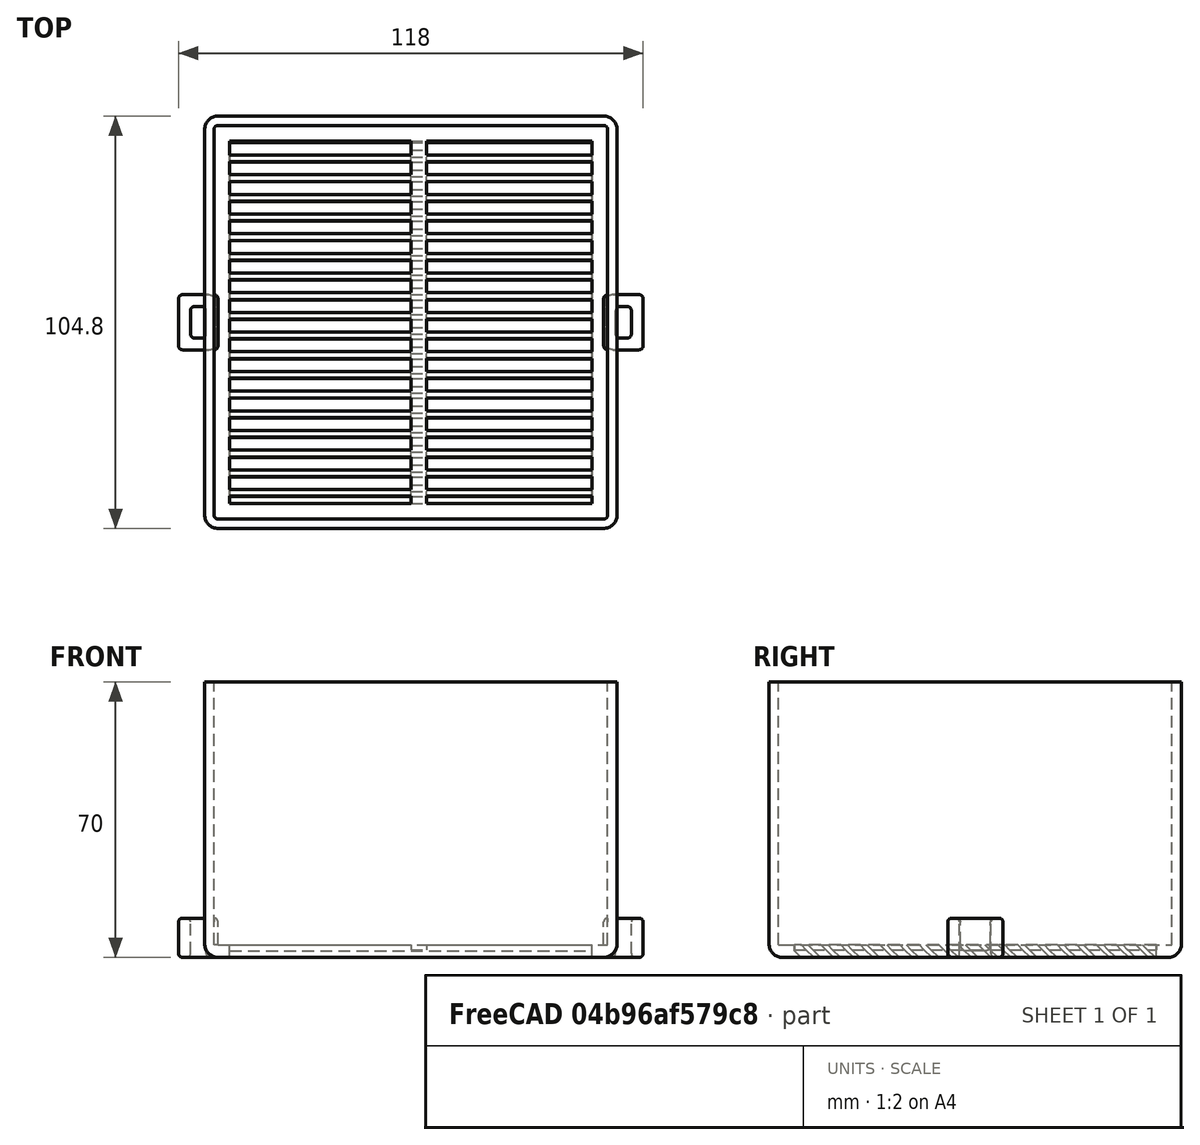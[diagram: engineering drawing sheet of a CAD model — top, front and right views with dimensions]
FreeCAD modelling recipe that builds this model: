
FCSTD DOCUMENT  (FreeCAD 0.17R13541 (Git))
Label: box_filter
License: All rights reserved
LicenseURL: http://en.wikipedia.org/wiki/All_rights_reserved
objects: Part::Box×30, Part::Cut×5, Part::MultiFuse×3, Part::Fillet×3
note: 41 computed .brp shape members not serialized (recipe doc carries the construction recipe); baked Part::Feature solids carry a one-line shape summary decoded from their .brp

FEATURE [Part::Box] Box  label="Cube"
  AttacherType = Attacher::AttachEngine3D
  Height = 70
  Length = 104.8
  Placement = pos=(-52.4,-52.4,0) rot=(0,0,1;0rad)
  Width = 104.8
FEATURE [Part::Box] Box001  label="Cube001"
  AttacherType = Attacher::AttachEngine3D
  Height = 70
  Length = 100
  Placement = pos=(-50,-50,3.2) rot=(0,0,1;0rad)
  Width = 100
FEATURE [Part::Box] Box002  label="Cube002"
  AttacherType = Attacher::AttachEngine3D
  Height = 80
  Length = 92
  Placement = pos=(-46,-46,-5) rot=(0,0,1;0rad)
  Width = 92
FEATURE [Part::Box] Box003  label="fin"
  AttacherType = Attacher::AttachEngine3D
  Height = 7
  Length = 104
  Placement = pos=(-52,0,-1) rot=(1,0,0;0.785398rad)
  Width = 1.2
FEATURE [Part::Cut] Cut
  Base = -> Box
  Tool = -> Box002
FEATURE [Part::Box] Box004  label="fin001"
  AttacherType = Attacher::AttachEngine3D
  Height = 7
  Length = 104
  Placement = pos=(-52,5,-1) rot=(1,0,0;0.785398rad)
  Width = 1.2
FEATURE [Part::Box] Box005  label="fin002"
  AttacherType = Attacher::AttachEngine3D
  Height = 7
  Length = 104
  Placement = pos=(-52,15,-1) rot=(1,0,0;0.785398rad)
  Width = 1.2
FEATURE [Part::Box] Box006  label="fin003"
  AttacherType = Attacher::AttachEngine3D
  Height = 7
  Length = 104
  Placement = pos=(-52,10,-1) rot=(1,0,0;0.785398rad)
  Width = 1.2
FEATURE [Part::Box] Box007  label="fin004"
  AttacherType = Attacher::AttachEngine3D
  Height = 7
  Length = 104
  Placement = pos=(-52,15,-1) rot=(1,0,0;0.785398rad)
  Width = 1.2
FEATURE [Part::Box] Box008  label="fin005"
  AttacherType = Attacher::AttachEngine3D
  Height = 7
  Length = 104
  Placement = pos=(-52,20,-1) rot=(1,0,0;0.785398rad)
  Width = 1.2
FEATURE [Part::Box] Box009  label="fin006"
  AttacherType = Attacher::AttachEngine3D
  Height = 7
  Length = 104
  Placement = pos=(-52,25,-1) rot=(1,0,0;0.785398rad)
  Width = 1.2
FEATURE [Part::Box] Box010  label="fin007"
  AttacherType = Attacher::AttachEngine3D
  Height = 7
  Length = 104
  Placement = pos=(-52,30,-1) rot=(1,0,0;0.785398rad)
  Width = 1.2
FEATURE [Part::Box] Box011  label="fin008"
  AttacherType = Attacher::AttachEngine3D
  Height = 7
  Length = 104
  Placement = pos=(-52,35,-1) rot=(1,0,0;0.785398rad)
  Width = 1.2
FEATURE [Part::Box] Box012  label="fin009"
  AttacherType = Attacher::AttachEngine3D
  Height = 7
  Length = 104
  Placement = pos=(-52,40,-1) rot=(1,0,0;0.785398rad)
  Width = 1.2
FEATURE [Part::Box] Box013  label="fin010"
  AttacherType = Attacher::AttachEngine3D
  Height = 7
  Length = 104
  Placement = pos=(-52,45,-1) rot=(1,0,0;0.785398rad)
  Width = 1.2
FEATURE [Part::Box] Box014  label="fint1"
  AttacherType = Attacher::AttachEngine3D
  Height = 7
  Length = 104
  Placement = pos=(-52,-45,-1) rot=(1,0,0;0.785398rad)
  Width = 1.2
FEATURE [Part::Box] Box015  label="fint002"
  AttacherType = Attacher::AttachEngine3D
  Height = 7
  Length = 104
  Placement = pos=(-52,-40,-1) rot=(1,0,0;0.785398rad)
  Width = 1.2
FEATURE [Part::Box] Box016  label="fint003"
  AttacherType = Attacher::AttachEngine3D
  Height = 7
  Length = 104
  Placement = pos=(-52,-35,-1) rot=(1,0,0;0.785398rad)
  Width = 1.2
FEATURE [Part::Box] Box017  label="fint004"
  AttacherType = Attacher::AttachEngine3D
  Height = 7
  Length = 104
  Placement = pos=(-52,-30,-1) rot=(1,0,0;0.785398rad)
  Width = 1.2
FEATURE [Part::Box] Box018  label="fint005"
  AttacherType = Attacher::AttachEngine3D
  Height = 7
  Length = 104
  Placement = pos=(-52,-20,-1) rot=(1,0,0;0.785398rad)
  Width = 1.2
FEATURE [Part::Box] Box019  label="fint006"
  AttacherType = Attacher::AttachEngine3D
  Height = 7
  Length = 104
  Placement = pos=(-52,-25,-1) rot=(1,0,0;0.785398rad)
  Width = 1.2
FEATURE [Part::Box] Box020  label="fint007"
  AttacherType = Attacher::AttachEngine3D
  Height = 7
  Length = 104
  Placement = pos=(-52,-20,-1) rot=(1,0,0;0.785398rad)
  Width = 1.2
FEATURE [Part::Box] Box021  label="fint008"
  AttacherType = Attacher::AttachEngine3D
  Height = 7
  Length = 104
  Placement = pos=(-52,-15,-1) rot=(1,0,0;0.785398rad)
  Width = 1.2
FEATURE [Part::Box] Box022  label="fint009"
  AttacherType = Attacher::AttachEngine3D
  Height = 7
  Length = 104
  Placement = pos=(-52,-10,-1) rot=(1,0,0;0.785398rad)
  Width = 1.2
FEATURE [Part::Box] Box023  label="fint010"
  AttacherType = Attacher::AttachEngine3D
  Height = 7
  Length = 104
  Placement = pos=(-52,-5,-1) rot=(1,0,0;0.785398rad)
  Width = 1.2
FEATURE [Part::MultiFuse] Fusion  label="fins"
  Shapes = -> [Box003,Box004,Box016,Box015,Box008,Box006,Box009,Box010,Box012,Box013,Box007,Box014,Box011,Box005,Box019,Box022,Box023,Box017,Box021,Box020,Box018]
FEATURE [Part::Box] Box024  label="Cube003"
  AttacherType = Attacher::AttachEngine3D
  Height = 10
  Length = 4
  Placement = pos=(0,-52,2) rot=(0,0,1;0rad)
  Width = 104
FEATURE [Part::MultiFuse] Fusion001
  Shapes = -> [Cut,Fusion,Box024]
FEATURE [Part::Cut] Cut001
  Base = -> Fusion001
  Tool = -> Box001
FEATURE [Part::Box] Box025  label="Cube004"
  AttacherType = Attacher::AttachEngine3D
  Height = 10
  Length = 120
  Placement = pos=(-60,-60,-10) rot=(0,0,1;0rad)
  Width = 120
FEATURE [Part::Cut] Cut002
  Base = -> Cut001
  Tool = -> Box025
FEATURE [Part::Fillet] Fillet
  Base = -> Cut002
  Edges = 12 edges: [Edge1 r=3.5,Edge3 r=3.5,Edge4 r=3.5,Edge5 r=3.5,Edge6 r=3.5,Edge14 r=3.5,Edge15 r=3.5,Edge170 r=3.5,Edge171 r=1,Edge172 r=1,Edge174 r=1,Edge176 r=1]
FEATURE [Part::Box] Box026  label="Cube005"
  AttacherType = Attacher::AttachEngine3D
  Height = 10
  Length = 10
  Placement = pos=(49,-7,0) rot=(0,0,1;0rad)
  Width = 14
FEATURE [Part::Box] Box027  label="Cube006"
  AttacherType = Attacher::AttachEngine3D
  Height = 14
  Length = 4
  Placement = pos=(52,-4,-1) rot=(0,0,1;0rad)
  Width = 8
FEATURE [Part::Cut] Cut003
  Base = -> Box026
  Tool = -> Box027
FEATURE [Part::Box] Box028  label="Cube007"
  AttacherType = Attacher::AttachEngine3D
  Height = 10
  Length = 10
  Placement = pos=(49,-7,0) rot=(0,0,1;0rad)
  Width = 14
FEATURE [Part::Box] Box029  label="Cube008"
  AttacherType = Attacher::AttachEngine3D
  Height = 14
  Length = 4
  Placement = pos=(52,-4,-1) rot=(0,0,1;0rad)
  Width = 8
FEATURE [Part::Cut] Cut004
  Base = -> Box028
  Placement = pos=(-108,0,0) rot=(0,0,1;0rad)
  Tool = -> Box029
FEATURE [Part::Fillet] Fillet001
  Base = -> Cut004
  Edges = 24 edges r=1: [Edge1,Edge2,Edge3,Edge4,Edge5,Edge6,Edge7,Edge8,Edge9,Edge10,Edge11,Edge12,Edge13,Edge14,Edge15,Edge16,Edge17,Edge18,Edge19,Edge20,Edge21,Edge22,Edge23,Edge24]
FEATURE [Part::Fillet] Fillet002
  Base = -> Cut003
  Edges = 24 edges r=1: [Edge1,Edge2,Edge3,Edge4,Edge5,Edge6,Edge7,Edge8,Edge9,Edge10,Edge11,Edge12,Edge13,Edge14,Edge15,Edge16,Edge17,Edge18,Edge19,Edge20,Edge21,Edge22,Edge23,Edge24]
FEATURE [Part::MultiFuse] Fusion002
  Shapes = -> [Fillet,Fillet001,Fillet002]
